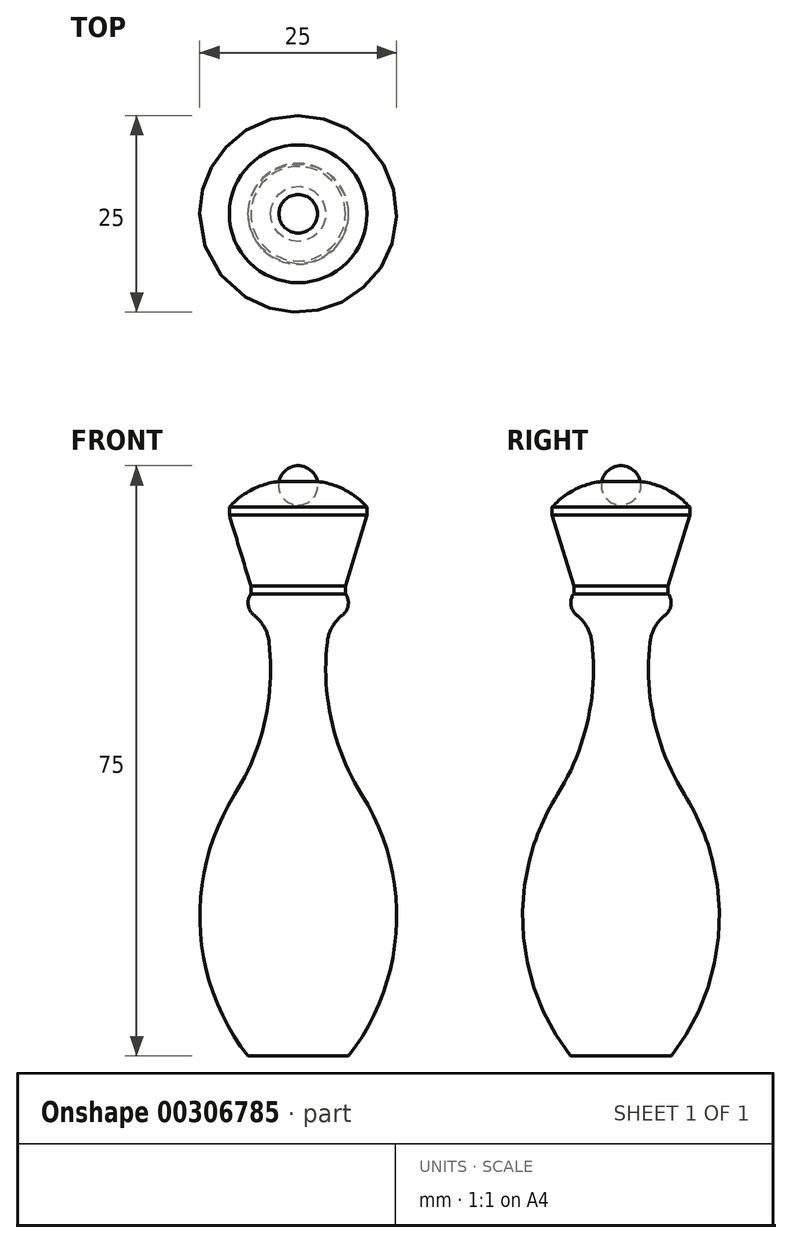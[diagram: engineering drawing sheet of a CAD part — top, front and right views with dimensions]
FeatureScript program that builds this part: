
annotation { "Feature Type Name" : "Feature", "Feature Type Description" : "" }
export const myFeature = defineFeature(function(context is Context, id is Id, definition is map)
    precondition{}
    {
        {
            var Q0;
            Q0=qCreatedBy(makeId("Front.planeOp"),FACE);
            var sketch = newSketch(context, id + "F0", { "sketchPlane" : qUnion([Q0])});
            skLineSegment(sketch, "E0", {"start": v(8.75, -5.27) * mm, "end": v(8.75, -6.27) * mm});
            skLineSegment(sketch, "E1", {"start": v(8.75, -6.27) * mm, "end": v(6, -15.27) * mm});
            skLineSegment(sketch, "E2", {"start": v(6, -15.27) * mm, "end": v(6, -16.27) * mm});
            skArc(sketch, "E3", {"start": v(4.2, -19.43) * mm, "mid": v(6.1, -18.43) * mm, "end": v(6, -16.27) * mm});
            skArc(sketch, "E4", {"start": v(4.2, -19.43) * mm, "mid": v(3.94, -30.98) * mm, "end": v(8.07, -41.78) * mm});
            skLineSegment(sketch, "E5", {"start": v(6.4, -75) * mm, "end": v(0, -75) * mm});
            skLineSegment(sketch, "E6", {"start": v(0, -75) * mm, "end": v(0, 0) * mm});
            skArc(sketch, "E7", {"start": v(6.4, -75) * mm, "mid": v(12.46, -58.66) * mm, "end": v(8.07, -41.78) * mm});
            skArc(sketch, "E8", {"start": v(2.45, -2) * mm, "mid": v(1.58, -0.56) * mm, "end": v(0, 0) * mm});
            skArc(sketch, "E9", {"start": v(8.75, -5.27) * mm, "mid": v(5.9, -3.06) * mm, "end": v(2.45, -2) * mm});
            skSolve(sketch);
        }
        {
            var Q0;
            Q0=makeQuery(id+"F0.imprint","IMPRINT",FACE,{"disambiguationData":[TD([[makeQuery(id+"F0.imprint","IMPRINT",EDGE,{"derivedFrom":sQuery(id+"F0.wireOp",EDGE,"E0")}),-1.0]])]});
            var Q1;
            Q1=sQuery(id+"F0.wireOp",EDGE,"E6");
            revolve(context, id + "F1", {"entities" : qUnion([Q0]), "axis" : qUnion([Q1]), "revolveType" : RevolveType.FULL});
        }
        {
            var Q0;
            Q0=makeQuery(id+"F1.opRevolve","SWEPT_EDGE",EDGE,{"disambiguationData":[OSD([sQuery(id+"F0.wireOp",EDGE,"E3"),sQuery(id+"F0.wireOp",EDGE,"E4")])]});
            fillet(context, id + "F2", {"entities" : qUnion([Q0]), "radius" : 5 * mm, "tangentPropagation" : true, "allowEdgeOverflow" : false});
        }
    });
